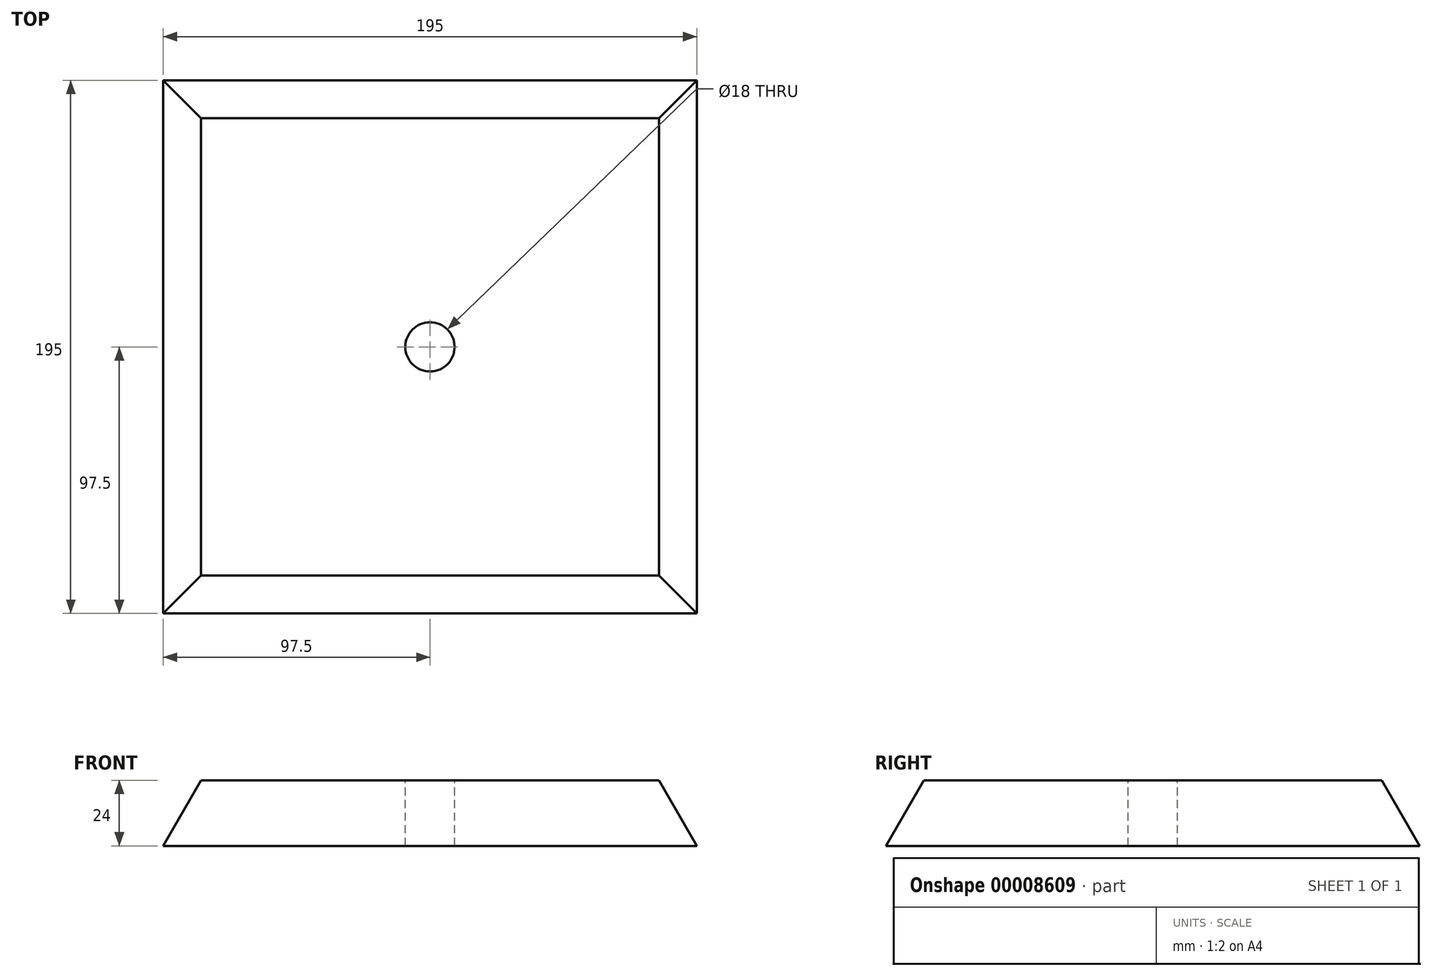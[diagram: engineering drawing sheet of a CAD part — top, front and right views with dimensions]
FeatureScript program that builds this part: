
annotation { "Feature Type Name" : "Feature", "Feature Type Description" : "" }
export const myFeature = defineFeature(function(context is Context, id is Id, definition is map)
    precondition{}
    {
        {
            var Q0;
            Q0=qCreatedBy(makeId("Top.planeOp"),FACE);
            var sketch = newSketch(context, id + "F0", { "sketchPlane" : qUnion([Q0])});
            skLineSegment(sketch, "E0.bottom", {"start": v(0, 0) * mm, "end": v(195, 0) * mm});
            skLineSegment(sketch, "E0.top", {"start": v(0, -195) * mm, "end": v(195, -195) * mm});
            skLineSegment(sketch, "E0.left", {"start": v(0, 0) * mm, "end": v(0, -195) * mm});
            skLineSegment(sketch, "E0.right", {"start": v(195, 0) * mm, "end": v(195, -195) * mm});
            skSolve(sketch);
        }
        {
            var Q0;
            Q0 = qSketchRegion(id + "F0", true);
            extrude(context, id + "F1", {"entities" : qUnion([Q0]), "depth" : 24 * mm, "hasDraft" : true, "draftAngle" : 30 * degree, "draftPullDirection" : true});
        }
        {
            var Q0;
            Q0=makeQuery(id+"F1.opExtrude","CAP_FACE",FACE,{"disambiguationData":[OSD([sQuery(id+"F0.wireOp",EDGE,"E0.bottom"),sQuery(id+"F0.wireOp",EDGE,"E0.top"),sQuery(id+"F0.wireOp",EDGE,"E0.left"),sQuery(id+"F0.wireOp",EDGE,"E0.right")])],"isStart":false});
            var sketch = newSketch(context, id + "F2", { "sketchPlane" : qUnion([Q0])});
            skCircle(sketch, "E1", {"center": v(97.5, -97.5) * mm, "radius": 9 * mm});
            skPoint(sketch, "E1.centerSnap0", {"position": v(181.14, -97.5) * mm});
            skPoint(sketch, "E1.centerSnap1", {"position": v(97.5, -13.86) * mm});
            skSolve(sketch);
        }
        {
            var Q0;
            Q0 = qSketchRegion(id + "F2", true);
            extrude(context, id + "F3", {"entities" : qUnion([Q0]), "operationType" : NewBodyOperationType.REMOVE, "oppositeDirection" : true, "depth" : 24 * mm});
        }
    });
